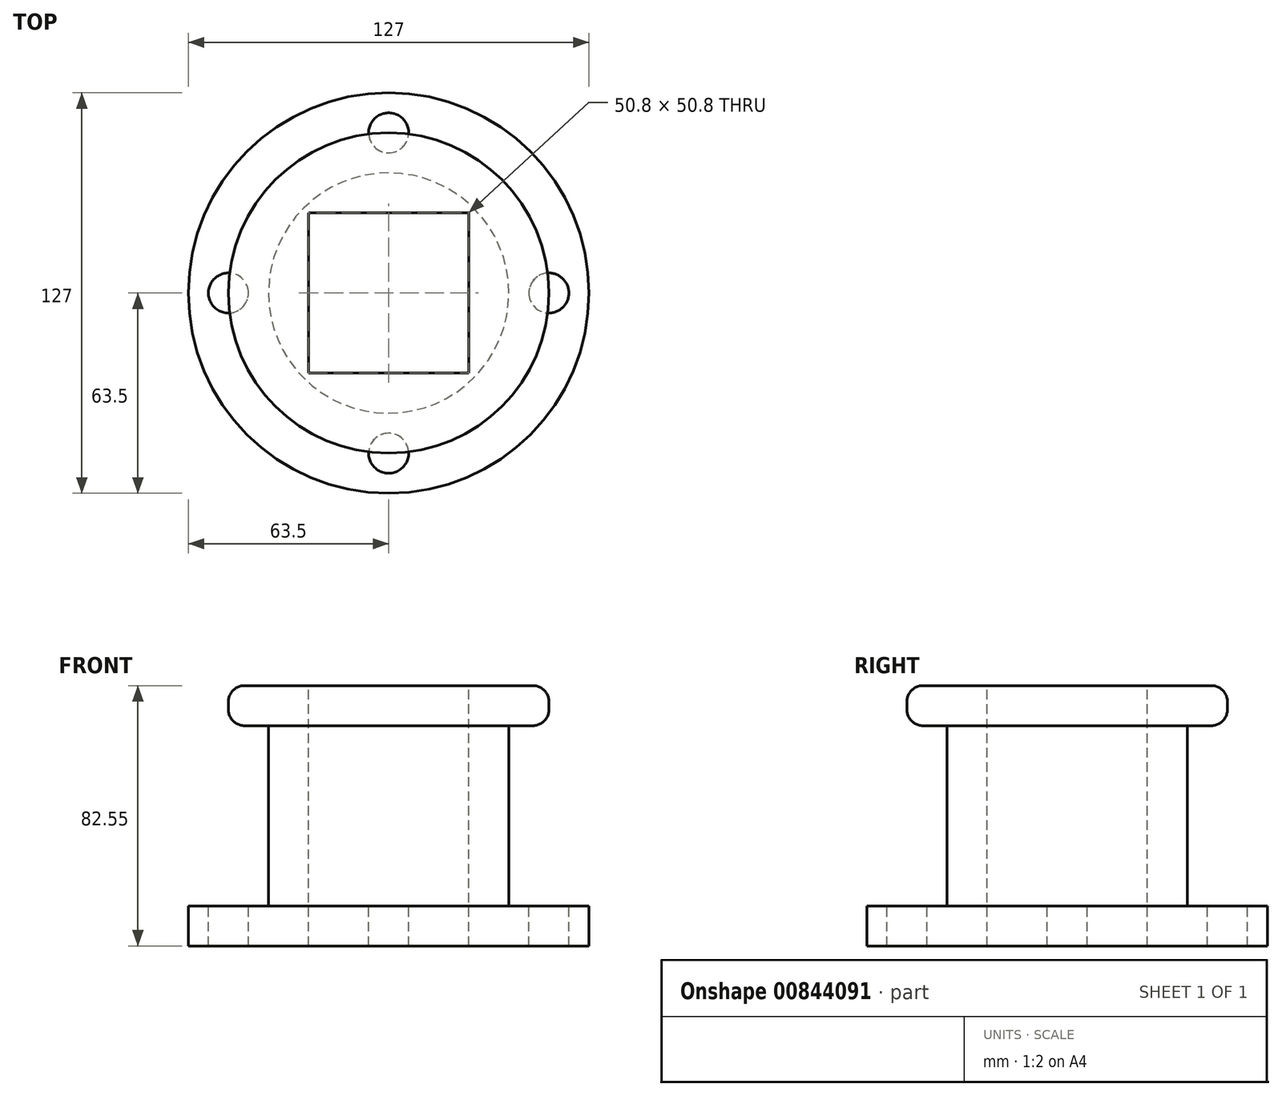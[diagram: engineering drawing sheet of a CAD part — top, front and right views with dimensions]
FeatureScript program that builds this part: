
annotation { "Feature Type Name" : "Feature", "Feature Type Description" : "" }
export const myFeature = defineFeature(function(context is Context, id is Id, definition is map)
    precondition{}
    {
        {
            var Q0;
            Q0=qCreatedBy(makeId("Top.planeOp"),FACE);
            var sketch = newSketch(context, id + "F0", { "sketchPlane" : qUnion([Q0])});
            skCircle(sketch, "E0", {"center": v(0, 0) * mm, "radius": 50.8 * mm});
            skSolve(sketch);
        }
        {
            var Q0;
            Q0 = qSketchRegion(id + "F0", true);
            extrude(context, id + "F1", {"entities" : qUnion([Q0]), "depth" : 12.7 * mm, "offsetDistance" : 25.4 * mm});
        }
        {
            var Q0;
            Q0=makeQuery(id+"F0.imprint","IMPRINT",FACE,{"disambiguationData":[TD([[makeQuery(id+"F0.imprint","IMPRINT",EDGE,{"derivedFrom":sQuery(id+"F0.wireOp",EDGE,"E0")}),1.0]])]});
            var sketch = newSketch(context, id + "F2", { "sketchPlane" : qUnion([Q0])});
            skCircle(sketch, "E1", {"center": v(0, 0) * mm, "radius": 38.1 * mm});
            skSolve(sketch);
        }
        {
            var Q0;
            Q0 = qSketchRegion(id + "F2", true);
            extrude(context, id + "F3", {"entities" : qUnion([Q0]), "operationType" : NewBodyOperationType.ADD, "oppositeDirection" : true, "depth" : 57.15 * mm, "offsetDistance" : 25.4 * mm});
        }
        {
            var Q0;
            Q0=makeQuery(id+"F3.opExtrude","CAP_FACE",FACE,{"disambiguationData":[OSD([sQuery(id+"F2.wireOp",EDGE,"E1")])],"isStart":false});
            var sketch = newSketch(context, id + "F4", { "sketchPlane" : qUnion([Q0])});
            skCircle(sketch, "E2", {"center": v(0, 0) * mm, "radius": 63.5 * mm});
            skSolve(sketch);
        }
        {
            var Q0;
            Q0 = qSketchRegion(id + "F4", true);
            extrude(context, id + "F5", {"entities" : qUnion([Q0]), "operationType" : NewBodyOperationType.ADD, "depth" : 12.7 * mm, "offsetDistance" : 25.4 * mm});
        }
        {
            var Q0;
            Q0=makeQuery(id+"F1.opExtrude","CAP_FACE",FACE,{"disambiguationData":[OSD([sQuery(id+"F0.wireOp",EDGE,"E0")])],"isStart":false});
            var sketch = newSketch(context, id + "F6", { "sketchPlane" : qUnion([Q0])});
            skLineSegment(sketch, "E3.bottom", {"start": v(-25.4, 25.4) * mm, "end": v(25.4, 25.4) * mm});
            skLineSegment(sketch, "E3.top", {"start": v(-25.4, -25.4) * mm, "end": v(25.4, -25.4) * mm});
            skLineSegment(sketch, "E3.left", {"start": v(-25.4, 25.4) * mm, "end": v(-25.4, -25.4) * mm});
            skLineSegment(sketch, "E3.right", {"start": v(25.4, 25.4) * mm, "end": v(25.4, -25.4) * mm});
            skPoint(sketch, "E3.middle", {"position": v(0, 0) * mm});
            skSolve(sketch);
        }
        {
            var Q0;
            Q0 = qSketchRegion(id + "F6", true);
            extrude(context, id + "F7", {"entities" : qUnion([Q0]), "operationType" : NewBodyOperationType.REMOVE, "oppositeDirection" : true, "depth" : 112.78 * mm, "offsetDistance" : 25.4 * mm});
        }
        {
            var Q0;
            Q0=makeQuery(id+"F5.opExtrude","CAP_FACE",FACE,{"disambiguationData":[OSD([sQuery(id+"F4.wireOp",EDGE,"E2")])],"isStart":true});
            var sketch = newSketch(context, id + "F8", { "sketchPlane" : qUnion([Q0])});
            skCircle(sketch, "E4", {"center": v(0, -50.8) * mm, "radius": 6.35 * mm});
            skCircle(sketch, "E5", {"center": v(50.8, 0) * mm, "radius": 6.35 * mm});
            skCircle(sketch, "E6", {"center": v(0, 50.8) * mm, "radius": 6.35 * mm});
            skCircle(sketch, "E7", {"center": v(-50.8, 0) * mm, "radius": 6.35 * mm});
            skSolve(sketch);
        }
        {
            var Q0;
            Q0 = qSketchRegion(id + "F8", true);
            extrude(context, id + "F9", {"entities" : qUnion([Q0]), "operationType" : NewBodyOperationType.REMOVE, "oppositeDirection" : true, "depth" : 25.4 * mm, "offsetDistance" : 25.4 * mm});
        }
        {
            var Q0;
            Q0=makeQuery(id+"F1.opExtrude","SWEPT_FACE",FACE,{"disambiguationData":[OSD([sQuery(id+"F0.wireOp",EDGE,"E0")])]});
            fillet(context, id + "F10", {"entities" : qUnion([Q0]), "radius" : 5.08 * mm, "tangentPropagation" : true, "allowEdgeOverflow" : false});
        }
    });
